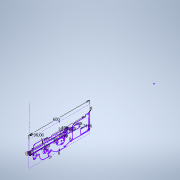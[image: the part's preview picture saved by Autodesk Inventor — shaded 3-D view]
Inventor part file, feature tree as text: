
AUTODESK INVENTOR PART (.ipt)
format: ipt  version: 2020 (Build 240168000, 168)  size: 239,616 bytes
history: native  units: mm
features: sketch x2, plane x1, other x1
ambient origin geometry x8: Origin, YZ Plane, XZ Plane, XY Plane, X Axis, Y Axis, Z Axis, Center Point
feature tree (4):
  sketch  "Sketch1"  dims[d24=600.0mm]
  plane  "Work Plane3"
  sketch  "Sketch2"  dims[d30=10.0mm d33=3.0mm d40=3.0mm d41=8.0mm d44=8.0mm d45=8.0mm d46=8.0mm d49=8.0mm d75=35.0mm d76=90.0deg d88=30.0mm d101=420.0mm d109=150.0mm d110=64.0mm d111=38.0mm d112=74.0mm d113=46.0mm d123=28.0mm d124=28.0mm d134=23.0mm d151=35.0mm d170=25.736954mm d171=400.0mm d187=25.0mm d200=25.0mm d201=340.0mm d232=340.0mm]
  other  "Image1"
